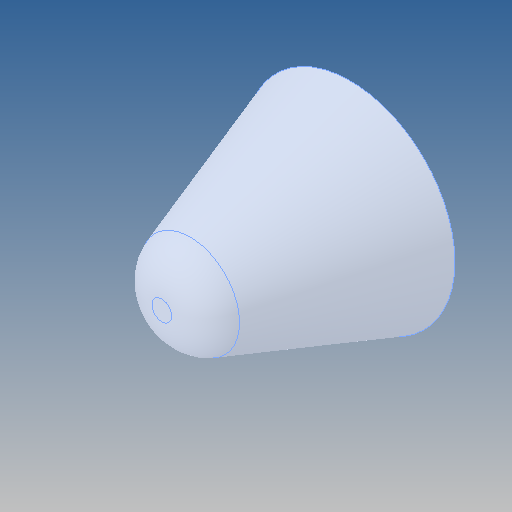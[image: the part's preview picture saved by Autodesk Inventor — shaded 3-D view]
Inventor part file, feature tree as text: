
AUTODESK INVENTOR PART (.ipt)
format: ipt  version: 2020 (Build 240168000, 168)  size: 111,616 bytes
history: mixed  units: mm
features: other x1, fillet x1, imported_body x1
ambient origin geometry x8: Origin, YZ Plane, XZ Plane, XY Plane, X Axis, Y Axis, Z Axis, Center Point
bodies: Body1 (imported_parasolid)
feature tree (3):
  other  "Твердое тело1"
  fillet  "Fillet1"  [1 undecoded]
  imported_body  NMx_Import_Brep_tag  [imported B-rep: ~4 faces, bbox_mm=[0.73655, 0.0, 0.9]]
note: 1 required parameter value undecoded (feature->parameter linkage not recoverable at this tier; creation-order binding heuristic only, values carry confidence <= 0.55)
